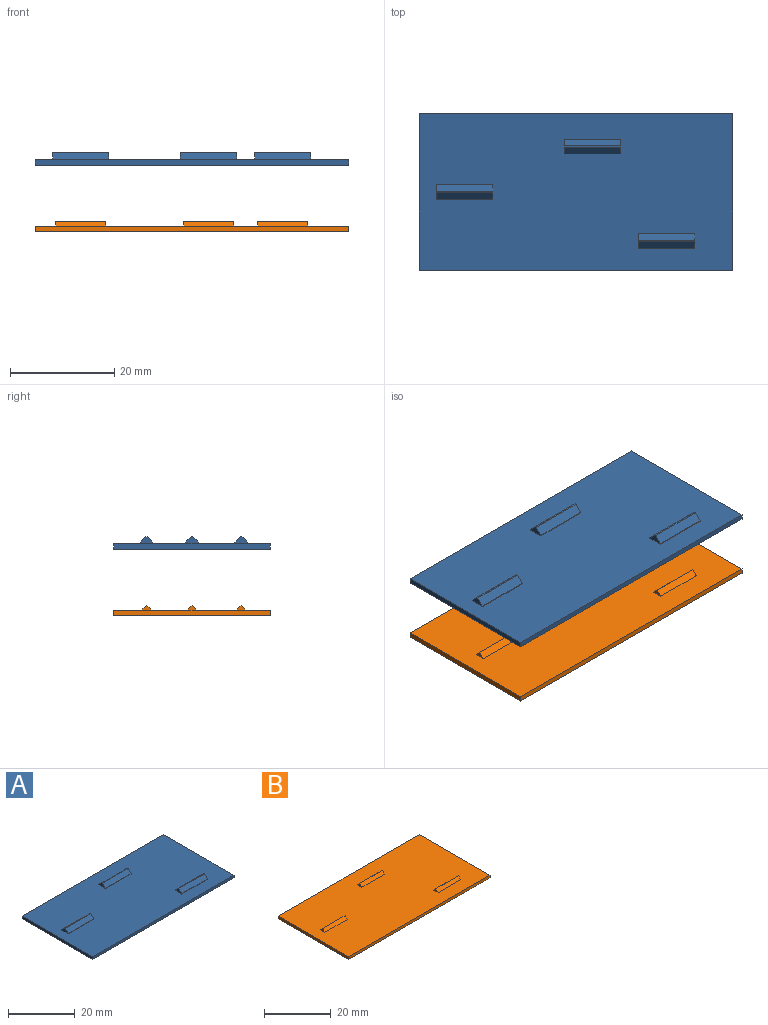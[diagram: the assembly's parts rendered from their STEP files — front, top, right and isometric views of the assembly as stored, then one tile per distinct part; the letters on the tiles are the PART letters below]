
ASSEMBLY  parts=2 mates=1
PART A: 42 faces, bbox 60x30x2.4 mm
  f0: plane 60x30mm, normal (0,0,1), area 1709.3mm2, adj f1,f2,f3,f4,f6,f7,f8,f9
  f1: plane 30x1mm, normal (1,0,0), area 30mm2, adj f0,f2,f4,f5
  f2: plane 60x1mm, normal (0,1,0), area 60mm2, adj f0,f1,f3,f5
  f3: plane 30x1mm, normal (-1,0,0), area 30mm2, adj f0,f2,f4,f5
  f4: plane 60x1mm, normal (0,-1,0), area 60mm2, adj f0,f1,f3,f5
  f5: plane 60x30mm, normal (0,0,-1), area 1800mm2, adj f1,f2,f3,f4
  f6: plane 10.8x0.14mm, normal (0,-1,0), area 1.5mm2, adj f0,f7,f9,f12
  f7: plane 2.8x1.4mm, normal (1,0,0), area 2.3mm2, adj f0,f6,f8,f10,f11,f12
  f8: plane 10.8x0.14mm, normal (0,1,0), area 1.5mm2, adj f0,f7,f9,f11
  f9: plane 2.8x1.4mm, normal (-1,0,0), area 2.3mm2, adj f0,f6,f8,f10,f11,f12
  f10: plane 10.8x0.28mm, normal (0,0,1), area 3mm2, adj f7,f9,f11,f12
  f11: plane 10.8x1.26mm, normal (0,0.71,0.71), area 19.2mm2, adj f7,f8,f9,f10
  f12: plane 10.8x1.26mm, normal (0,-0.71,0.71), area 19.2mm2, adj f6,f7,f9,f10
  f13: plane 10.8x0.14mm, normal (0,-1,0), area 1.5mm2, adj f0,f14,f16,f19
  f14: plane 2.8x1.4mm, normal (1,0,0), area 2.3mm2, adj f0,f13,f15,f17,f18,f19
  f15: plane 10.8x0.14mm, normal (0,1,0), area 1.5mm2, adj f0,f14,f16,f18
  f16: plane 2.8x1.4mm, normal (-1,0,0), area 2.3mm2, adj f0,f13,f15,f17,f18,f19
  f17: plane 10.8x0.28mm, normal (0,0,1), area 3mm2, adj f14,f16,f18,f19
  f18: plane 10.8x1.26mm, normal (0,0.71,0.71), area 19.2mm2, adj f14,f15,f16,f17
  f19: plane 10.8x1.26mm, normal (0,-0.71,0.71), area 19.2mm2, adj f13,f14,f16,f17
  f20: plane 10.8x0.14mm, normal (0,-1,0), area 1.5mm2, adj f0,f21,f23,f26
  f21: plane 2.8x1.4mm, normal (1,0,0), area 2.3mm2, adj f0,f20,f22,f24,f25,f26
  f22: plane 10.8x0.14mm, normal (0,1,0), area 1.5mm2, adj f0,f21,f23,f25
  f23: plane 2.8x1.4mm, normal (-1,0,0), area 2.3mm2, adj f0,f20,f22,f24,f25,f26
  f24: plane 10.8x0.28mm, normal (0,0,1), area 3mm2, adj f21,f23,f25,f26
  f25: plane 10.8x1.26mm, normal (0,0.71,0.71), area 19.2mm2, adj f21,f22,f23,f24
  f26: plane 10.8x1.26mm, normal (0,-0.71,0.71), area 19.2mm2, adj f20,f21,f23,f24
  f27: plane 2x1mm, normal (-1,0,0), area 1mm2, adj f29,f30,f31
  f28: plane 2x1mm, normal (1,0,0), area 1mm2, adj f29,f30,f31
  f29: plane 10x2mm, normal (0,0,1), area 20mm2, adj f27,f28,f30,f31
  f30: plane 10x1mm, normal (0,0.71,-0.71), area 14.1mm2, adj f27,f28,f29,f31
  f31: plane 10x1mm, normal (0,-0.71,-0.71), area 14.1mm2, adj f27,f28,f29,f30
  f32: plane 2x1mm, normal (-1,0,0), area 1mm2, adj f34,f35,f36
  f33: plane 2x1mm, normal (1,0,0), area 1mm2, adj f34,f35,f36
  f34: plane 10x2mm, normal (0,0,1), area 20mm2, adj f32,f33,f35,f36
  f35: plane 10x1mm, normal (0,0.71,-0.71), area 14.1mm2, adj f32,f33,f34,f36
  f36: plane 10x1mm, normal (0,-0.71,-0.71), area 14.1mm2, adj f32,f33,f34,f35
  f37: plane 2x1mm, normal (-1,0,0), area 1mm2, adj f39,f40,f41
  f38: plane 2x1mm, normal (1,0,0), area 1mm2, adj f39,f40,f41
  f39: plane 10x2mm, normal (0,0,1), area 20mm2, adj f37,f38,f40,f41
  f40: plane 10x1mm, normal (0,0.71,-0.71), area 14.1mm2, adj f37,f38,f39,f41
  f41: plane 10x1mm, normal (0,-0.71,-0.71), area 14.1mm2, adj f37,f38,f39,f40
PART B: 18 faces, bbox 60x30x2 mm
  f0: plane 30x1mm, normal (1,0,0), area 30mm2, adj f1,f3,f4,f5
  f1: plane 60x1mm, normal (0,1,0), area 60mm2, adj f0,f2,f4,f5
  f2: plane 30x1mm, normal (-1,0,0), area 30mm2, adj f1,f3,f4,f5
  f3: plane 60x1mm, normal (0,-1,0), area 60mm2, adj f0,f2,f4,f5
  f4: plane 60x30mm, normal (0,0,-1), area 1800mm2, adj f0,f1,f2,f3
  f5: plane 60x30mm, normal (0,0,1), area 1745.3mm2, adj f0,f1,f2,f3,f6,f7,f8,f9
  f6: plane 1.9x0.95mm, normal (1,0,0), area 0.9mm2, adj f5,f8,f9
  f7: plane 1.9x0.95mm, normal (-1,0,0), area 0.9mm2, adj f5,f8,f9
  f8: plane 9.6x0.95mm, normal (0,-0.71,0.71), area 12.9mm2, adj f5,f6,f7,f9
  f9: plane 9.6x0.95mm, normal (0,0.71,0.71), area 12.9mm2, adj f5,f6,f7,f8
  f10: plane 1.9x0.95mm, normal (1,0,0), area 0.9mm2, adj f5,f12,f13
  f11: plane 1.9x0.95mm, normal (-1,0,0), area 0.9mm2, adj f5,f12,f13
  f12: plane 9.6x0.95mm, normal (0,-0.71,0.71), area 12.9mm2, adj f5,f10,f11,f13
  f13: plane 9.6x0.95mm, normal (0,0.71,0.71), area 12.9mm2, adj f5,f10,f11,f12
  f14: plane 1.9x0.95mm, normal (1,0,0), area 0.9mm2, adj f5,f16,f17
  f15: plane 1.9x0.95mm, normal (-1,0,0), area 0.9mm2, adj f5,f16,f17
  f16: plane 9.6x0.95mm, normal (0,-0.71,0.71), area 12.9mm2, adj f5,f14,f15,f17
  f17: plane 9.6x0.95mm, normal (0,0.71,0.71), area 12.9mm2, adj f5,f14,f15,f16
PLACE A t=(9.47,9.95,15.64)mm
PLACE B rot(axis=(0,0,1),0deg) t=(9.47,9.95,3.94)mm
MATE slider A.f5 <-> B.f5  axis (0,0,1) through (9.47,9.95,15.64)mm
